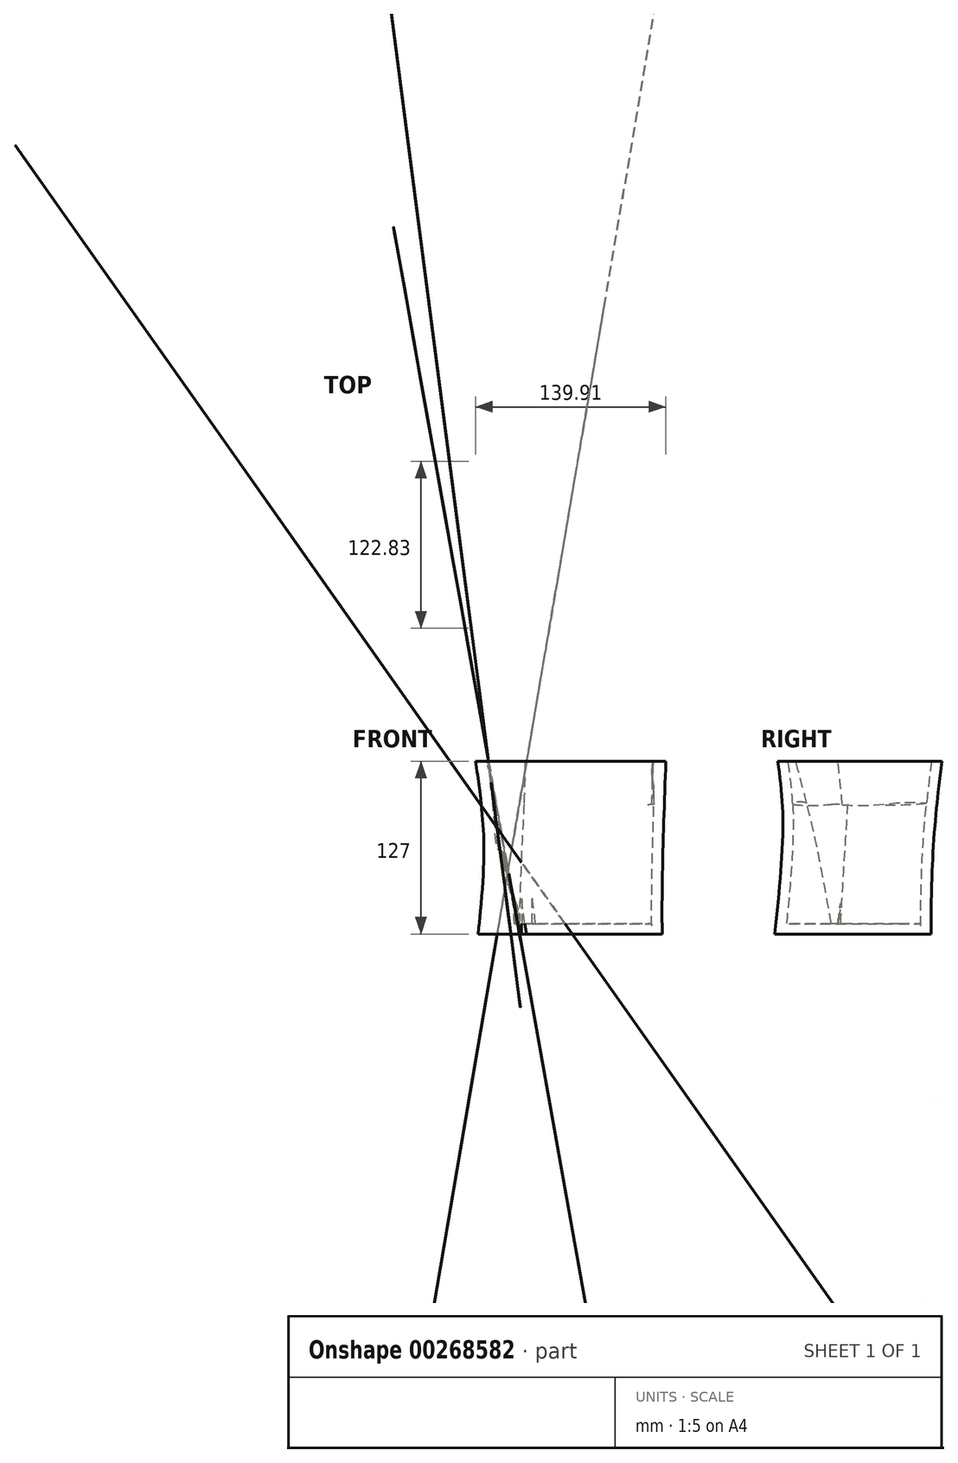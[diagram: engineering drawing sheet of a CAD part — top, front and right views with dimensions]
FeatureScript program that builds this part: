
annotation { "Feature Type Name" : "Feature", "Feature Type Description" : "" }
export const myFeature = defineFeature(function(context is Context, id is Id, definition is map)
    precondition{}
    {
        {
            var Q0;
            Q0=qCreatedBy(makeId("Top.planeOp"),FACE);
            cPlane(context, id + "F0", {"entities" : qUnion([Q0]), "cplaneType" : CPlaneType.OFFSET, "offset" : 127 * mm, "width" : 152.4 * mm, "height" : 152.4 * mm});
        }
        {
            var Q0;
            Q0=qCreatedBy(makeId("Top.planeOp"),FACE);
            var sketch = newSketch(context, id + "F1", { "sketchPlane" : qUnion([Q0])});
            skFitSpline(sketch, "E0", {"points": [v(-35.9, 28.01) * mm, v(0, 47.2) * mm, v(17.95, 20.27) * mm, v(23.52, 16.25) * mm, v(61.6, 8.51) * mm, v(51.69, -44.73) * mm, v(7.43, -65.15) * mm, v(-13.62, -38.23) * mm, v(-62.83, -30.8) * mm, v(-68.1, -28.32) * mm, v(-34.36, -4.8) * mm, v(-35.9, 28.01) * mm]});
            skSolve(sketch);
        }
        {
            var Q0;
            Q0=qCreatedBy(id+"F0.planeOp",FACE);
            var sketch = newSketch(context, id + "F2", { "sketchPlane" : qUnion([Q0])});
            skFitSpline(sketch, "E1", {"points": [v(-51.07, 6.96) * mm, v(-22.6, 22.44) * mm, v(-7.43, 54.63) * mm, v(37.14, 36.06) * mm, v(42.71, 6.96) * mm, v(69.64, -22.44) * mm, v(35.6, -43.8) * mm, v(10.52, -61.13) * mm, v(-38.38, -58.34) * mm, v(-44.57, -35.75) * mm, v(-69.95, -14.4) * mm, v(-51.07, 6.96) * mm]});
            skSolve(sketch);
        }
        {
            var Q0;
            Q0=makeQuery(id+"F1.imprint","IMPRINT",FACE,{"disambiguationData":[TD([[makeQuery(id+"F1.imprint","IMPRINT",EDGE,{"derivedFrom":sQuery(id+"F1.wireOp",EDGE,"E0")}),-1.0]])]});
            var Q1;
            Q1=makeQuery(id+"F2.imprint","IMPRINT",FACE,{"disambiguationData":[TD([[makeQuery(id+"F2.imprint","IMPRINT",EDGE,{"derivedFrom":sQuery(id+"F2.wireOp",EDGE,"E1")}),-1.0]])]});
            loft(context, id + "F3", {"sheetProfilesArray" : [{ "sheetProfileEntities" : qUnion([Q0]) }, { "sheetProfileEntities" : qUnion([Q1]) }]});
        }
        {
            var Q0;
            Q0=makeQuery(id+"F3.opLoft","CAP_FACE",FACE,{"disambiguationData":[OSD([makeQuery(id+"F2.imprint","IMPRINT",FACE,{"disambiguationData":[TD([[makeQuery(id+"F2.imprint","IMPRINT",EDGE,{"derivedFrom":sQuery(id+"F2.wireOp",EDGE,"E1")}),-1.0]])]})])],"isStart":true});
            shell(context, id + "F4", {"entities" : qUnion([Q0]), "thickness" : 7.62 * mm});
        }
    });
